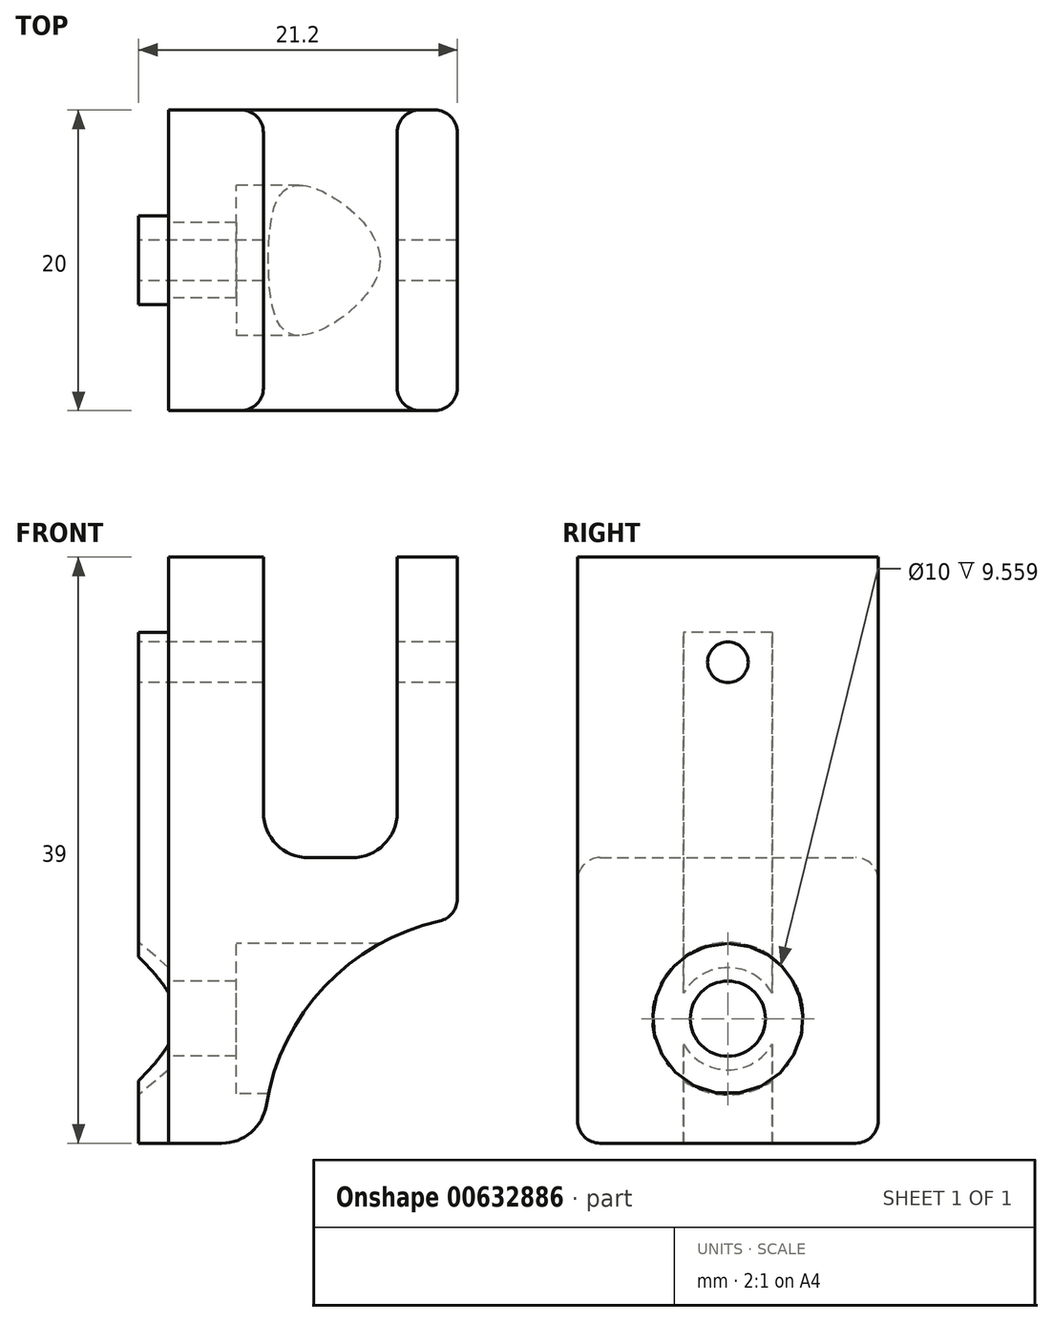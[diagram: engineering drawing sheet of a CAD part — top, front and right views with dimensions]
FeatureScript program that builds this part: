
annotation { "Feature Type Name" : "Feature", "Feature Type Description" : "" }
export const myFeature = defineFeature(function(context is Context, id is Id, definition is map)
    precondition{}
    {
        {
            var Q0;
            Q0=qCreatedBy(makeId("Front.planeOp"),FACE);
            var sketch = newSketch(context, id + "F0", { "sketchPlane" : qUnion([Q0])});
            skLineSegment(sketch, "E0.bottom", {"start": v(0, 0) * mm, "end": v(6.3, 0) * mm});
            skLineSegment(sketch, "E0.right", {"start": v(6.3, 0) * mm, "end": v(6.3, 15) * mm});
            skLineSegment(sketch, "E1.bottom", {"start": v(15.2, 39) * mm, "end": v(19.2, 39) * mm});
            skLineSegment(sketch, "E1.left", {"start": v(15.2, 39) * mm, "end": v(15.2, 19) * mm});
            skLineSegment(sketch, "E2.bottom", {"start": v(15.2, 19) * mm, "end": v(6.3, 19) * mm});
            skLineSegment(sketch, "E2.top", {"start": v(19.2, 15) * mm, "end": v(6.3, 15) * mm});
            skLineSegment(sketch, "E3", {"start": v(19.2, 39) * mm, "end": v(19.2, 15) * mm});
            skLineSegment(sketch, "E4", {"start": v(6.3, 19) * mm, "end": v(6.3, 39) * mm});
            skLineSegment(sketch, "E5", {"start": v(6.3, 39) * mm, "end": v(0, 39) * mm});
            skLineSegment(sketch, "E6", {"start": v(0, 39) * mm, "end": v(0, 0) * mm});
            skSolve(sketch);
        }
        {
            var Q0;
            {var subQ1=sQuery(id+"F0.wireOp",EDGE,"E0.bottom");Q0=makeQuery(id+"F0.imprint","IMPRINT",FACE,{"disambiguationData":[TD([[makeQuery(id+"F0.imprint","IMPRINT",EDGE,{"derivedFrom":subQ1}),1.0]])]});}
            var Q1;
            Q1=makeQuery(id+"F0.imprint","IMPRINT",FACE,{"disambiguationData":[TD([[makeQuery(id+"F0.imprint","IMPRINT",EDGE,{"derivedFrom":sQuery(id+"F0.wireOp",EDGE,"E2.top")}),-1.0]])]});
            var Q2;
            Q2=makeQuery(id+"F0.imprint","IMPRINT",FACE,{"disambiguationData":[TD([[makeQuery(id+"F0.imprint","IMPRINT",EDGE,{"derivedFrom":sQuery(id+"F0.wireOp",EDGE,"E1.bottom")}),-1.0]])]});
            extrude(context, id + "F1", {"entities" : qUnion([Q0, Q1, Q2]), "depth" : 10 * mm, "hasSecondDirection" : true, "secondDirectionOppositeDirection" : true, "secondDirectionDepth" : 10 * mm, "offsetDistance" : 25 * mm});
        }
        {
            var Q0;
            Q0=makeQuery(id+"F1.opExtrude","SWEPT_EDGE",EDGE,{"disambiguationData":[OSD([sQuery(id+"F0.wireOp",EDGE,"E0.right"),sQuery(id+"F0.wireOp",EDGE,"E2.top"),sQuery(id+"F0.wireOp",EDGE,"E2.right")])]});
            fillet(context, id + "F2", {"entities" : qUnion([Q0]), "radius" : 15 * mm, "tangentPropagation" : true, "allowEdgeOverflow" : false});
        }
        {
            var Q0;
            Q0=makeQuery(id+"F1.opExtrude","SWEPT_EDGE",EDGE,{"disambiguationData":[OSD([sQuery(id+"F0.wireOp",EDGE,"E0.right"),sQuery(id+"F0.wireOp",EDGE,"E2.bottom"),sQuery(id+"F0.wireOp",EDGE,"E2.right")])]});
            var Q1;
            Q1=makeQuery(id+"F1.opExtrude","SWEPT_EDGE",EDGE,{"disambiguationData":[OSD([sQuery(id+"F0.wireOp",EDGE,"E1.left"),sQuery(id+"F0.wireOp",EDGE,"E2.bottom")])]});
            fillet(context, id + "F3", {"entities" : qUnion([Q0, Q1]), "radius" : 3 * mm, "tangentPropagation" : true, "allowEdgeOverflow" : false});
        }
        {
            var Q0;
            Q0=qCreatedBy(makeId("Top.planeOp"),FACE);
            var sketch = newSketch(context, id + "F4", { "sketchPlane" : qUnion([Q0])});
            skLineSegment(sketch, "E7.bottom", {"start": v(-2, 2.95) * mm, "end": v(2, 2.95) * mm});
            skLineSegment(sketch, "E7.top", {"start": v(-2, -2.95) * mm, "end": v(2, -2.95) * mm});
            skLineSegment(sketch, "E7.left", {"start": v(-2, 2.95) * mm, "end": v(-2, -2.95) * mm});
            skLineSegment(sketch, "E7.right", {"start": v(2, 2.95) * mm, "end": v(2, -2.95) * mm});
            skPoint(sketch, "E7.middle", {"position": v(0, 0) * mm});
            skSolve(sketch);
        }
        {
            var Q0;
            Q0=makeQuery(id+"F4.imprint","IMPRINT",FACE,{"disambiguationData":[TD([[makeQuery(id+"F4.imprint","IMPRINT",EDGE,{"derivedFrom":sQuery(id+"F4.wireOp",EDGE,"E7.bottom")}),-1.0]])]});
            extrude(context, id + "F5", {"entities" : qUnion([Q0]), "operationType" : NewBodyOperationType.ADD, "depth" : 34 * mm, "offsetDistance" : 25 * mm});
        }
        {
            var Q0;
            Q0=qCreatedBy(makeId("Right.planeOp"),FACE);
            var sketch = newSketch(context, id + "F6", { "sketchPlane" : qUnion([Q0])});
            skCircle(sketch, "E8", {"center": v(0, 32) * mm, "radius": 1.35 * mm});
            skCircle(sketch, "E9", {"center": v(0, 8.28) * mm, "radius": 2.5 * mm});
            skCircle(sketch, "E10", {"center": v(0, 8.28) * mm, "radius": 5 * mm});
            skCircle(sketch, "E11", {"center": v(0, 8.28) * mm, "radius": 3.4 * mm});
            skSolve(sketch);
        }
        {
            var Q0;
            Q0=makeQuery(id+"F6.imprint","IMPRINT",FACE,{"disambiguationData":[TD([[makeQuery(id+"F6.imprint","IMPRINT",EDGE,{"derivedFrom":sQuery(id+"F6.wireOp",EDGE,"E8")}),1.0]])]});
            extrude(context, id + "F7", {"entities" : qUnion([Q0]), "operationType" : NewBodyOperationType.REMOVE, "depth" : 25 * mm, "hasSecondDirection" : true, "secondDirectionOppositeDirection" : true, "secondDirectionDepth" : 25 * mm});
        }
        {
            var Q0;
            Q0=makeQuery(id+"F6.imprint","IMPRINT",FACE,{"disambiguationData":[TD([[makeQuery(id+"F6.imprint","IMPRINT",EDGE,{"derivedFrom":sQuery(id+"F6.wireOp",EDGE,"E9")}),1.0]])]});
            extrude(context, id + "F8", {"entities" : qUnion([Q0]), "operationType" : NewBodyOperationType.REMOVE, "depth" : 15 * mm, "hasSecondDirection" : true, "secondDirectionOppositeDirection" : true, "secondDirectionDepth" : 10 * mm});
        }
        {
            var Q0;
            Q0=makeQuery(id+"F6.imprint","IMPRINT",FACE,{"disambiguationData":[TD([[makeQuery(id+"F6.imprint","IMPRINT",EDGE,{"derivedFrom":sQuery(id+"F6.wireOp",EDGE,"E9")}),-1.0]])]});
            var Q1;
            Q1=makeQuery(id+"F6.imprint","IMPRINT",FACE,{"disambiguationData":[TD([[makeQuery(id+"F6.imprint","IMPRINT",EDGE,{"derivedFrom":sQuery(id+"F6.wireOp",EDGE,"E10")}),1.0]])]});
            extrude(context, id + "F9", {"entities" : qUnion([Q0, Q1]), "operationType" : NewBodyOperationType.REMOVE, "depth" : 30 * mm, "hasSecondDirection" : true, "secondDirectionOppositeDirection" : false, "secondDirectionDepth" : 4.5 * mm, "offsetDistance" : 25 * mm});
        }
        {
            var Q0;
            Q0=makeQuery(id+"F6.imprint","IMPRINT",FACE,{"disambiguationData":[TD([[makeQuery(id+"F6.imprint","IMPRINT",EDGE,{"derivedFrom":sQuery(id+"F6.wireOp",EDGE,"E9")}),-1.0]])]});
            extrude(context, id + "F10", {"entities" : qUnion([Q0]), "operationType" : NewBodyOperationType.REMOVE, "oppositeDirection" : true, "depth" : 10 * mm, "hasDraft" : true, "draftAngle" : 40 * degree, "offsetDistance" : 25 * mm});
        }
        {
            var Q0;
            Q0=makeQuery(id+"FVQzFijdfIberP7_1.boolean.opBoolean","INTERSECT",EDGE,{"derivedFrom":[makeQuery(id+"F1.opExtrude","SWEPT_FACE",FACE,{"disambiguationData":[OSD([sQuery(id+"F0.wireOp",EDGE,"E1.bottom")])]}),makeQuery(id+"FVQzFijdfIberP7_1.opExtrude","SWEPT_FACE",FACE,{"disambiguationData":[OSD([sQuery(id+"FllVCIRI6JCQqES_1.wireOp",EDGE,"0gJeJJ1y-EJvm-fnZg-GKMm-UuW6JYeC1a1f")])]})]});
            var Q1;
            Q1=makeQuery(id+"F1.opExtrude","CAP_EDGE",EDGE,{"disambiguationData":[OSD([sQuery(id+"F0.wireOp",EDGE,"E0.top")])],"isStart":true});
            var Q2;
            Q2=makeQuery(id+"FVQzFijdfIberP7_1.boolean.opBoolean","INTERSECT",EDGE,{"derivedFrom":[makeQuery(id+"F1.opExtrude","SWEPT_FACE",FACE,{"disambiguationData":[OSD([sQuery(id+"F0.wireOp",EDGE,"E1.bottom")])]}),makeQuery(id+"FVQzFijdfIberP7_1.opExtrude","SWEPT_FACE",FACE,{"disambiguationData":[OSD([sQuery(id+"FllVCIRI6JCQqES_1.wireOp",EDGE,"ad4fdd70-2fb9-4313-b07b-df9d61838bc60.MirrorCS")])]})]});
            var Q3;
            Q3=makeQuery(id+"F1.opExtrude","CAP_EDGE",EDGE,{"disambiguationData":[OSD([sQuery(id+"F0.wireOp",EDGE,"E0.top")])],"isStart":false});
            var Q4;
            Q4=makeQuery(id+"F1.opExtrude","CAP_EDGE",EDGE,{"disambiguationData":[OSD([sQuery(id+"F0.wireOp",EDGE,"E0.bottom")])],"isStart":true});
            var Q5;
            Q5=makeQuery(id+"F1.opExtrude","CAP_EDGE",EDGE,{"disambiguationData":[OSD([sQuery(id+"F0.wireOp",EDGE,"E0.bottom")])],"isStart":false});
            var Q6;
            Q6=makeQuery(id+"F2.opFillet","BLEND_EDGE",EDGE,{"blendedFrom":[makeQuery(id+"F1.opExtrude","SWEPT_EDGE",EDGE,{"disambiguationData":[OSD([sQuery(id+"F0.wireOp",EDGE,"E0.right"),sQuery(id+"F0.wireOp",EDGE,"E2.top"),sQuery(id+"F0.wireOp",EDGE,"E2.right")])]}),makeQuery(id+"F1.opExtrude","SWEPT_FACE",FACE,{"disambiguationData":[OSD([sQuery(id+"F0.wireOp",EDGE,"E1.right"),sQuery(id+"F0.wireOp",EDGE,"E2.left")])]})],"blendedInto":[makeQuery(id+"F1.opExtrude","SWEPT_FACE",FACE,{"disambiguationData":[OSD([sQuery(id+"F0.wireOp",EDGE,"E1.right"),sQuery(id+"F0.wireOp",EDGE,"E2.left")])]})]});
            var Q7;
            Q7=makeQuery(id+"FVQzFijdfIberP7_1.boolean.opBoolean","INTERSECT",EDGE,{"derivedFrom":[makeQuery(id+"F2.opFillet","BLEND_FACE",FACE,{"disambiguationData":[OSD([sQuery(id+"F0.wireOp",EDGE,"E0.right"),sQuery(id+"F0.wireOp",EDGE,"E2.top"),sQuery(id+"F0.wireOp",EDGE,"E2.right")])]}),makeQuery(id+"FVQzFijdfIberP7_1.opExtrude","SWEPT_FACE",FACE,{"disambiguationData":[OSD([sQuery(id+"FllVCIRI6JCQqES_1.wireOp",EDGE,"ad4fdd70-2fb9-4313-b07b-df9d61838bc60.MirrorCS")])]})]});
            var Q8;
            Q8=makeQuery(id+"FVQzFijdfIberP7_1.boolean.opBoolean","COPY",EDGE,{"derivedFrom":makeQuery(id+"FVQzFijdfIberP7_1.opExtrude","SWEPT_EDGE",EDGE,{"disambiguationData":[OSD([sQuery(id+"FllVCIRI6JCQqES_1.wireOp",EDGE,"ad4fdd70-2fb9-4313-b07b-df9d61838bc60.MirrorCS"),sQuery(id+"FllVCIRI6JCQqES_1.wireOp",EDGE,"6d596fc3-1ca0-40c5-aee4-fe9f60dd68ae0.MirrorCS")])]})});
            var Q9;
            Q9=makeQuery(id+"FVQzFijdfIberP7_1.boolean.opBoolean","COPY",EDGE,{"derivedFrom":makeQuery(id+"FVQzFijdfIberP7_1.opExtrude","SWEPT_EDGE",EDGE,{"disambiguationData":[OSD([sQuery(id+"FllVCIRI6JCQqES_1.wireOp",EDGE,"0gJeJJ1y-EJvm-fnZg-GKMm-UuW6JYeC1a1f"),sQuery(id+"FllVCIRI6JCQqES_1.wireOp",EDGE,"ayhZilKi-yUaR-i3xm-yCP8-kIRGACUT5FV1")])]})});
            var Q10;
            Q10=makeQuery(id+"FVQzFijdfIberP7_1.boolean.opBoolean","INTERSECT",EDGE,{"derivedFrom":[makeQuery(id+"F2.opFillet","BLEND_FACE",FACE,{"disambiguationData":[OSD([sQuery(id+"F0.wireOp",EDGE,"E0.right"),sQuery(id+"F0.wireOp",EDGE,"E2.top"),sQuery(id+"F0.wireOp",EDGE,"E2.right")])]}),makeQuery(id+"FVQzFijdfIberP7_1.opExtrude","SWEPT_FACE",FACE,{"disambiguationData":[OSD([sQuery(id+"FllVCIRI6JCQqES_1.wireOp",EDGE,"0gJeJJ1y-EJvm-fnZg-GKMm-UuW6JYeC1a1f")])]})]});
            var Q11;
            {var subQ0=sQuery(id+"F0.wireOp",EDGE,"E0.right");Q11=makeQuery(id+"F1.opExtrude","CAP_EDGE",EDGE,{"disambiguationData":[OSD([subQ0]),TDD([makeQuery(id+"F0.imprint","IMPRINT",EDGE,{"disambiguationData":[TD([[makeQuery(id+"F0.imprint","INTERSECT",VERTEX,{"derivedFrom":[sQuery(id+"F0.wireOp",EDGE,"E0.top"),subQ0]}),1.0]])],"derivedFrom":subQ0})])],"isStart":false});}
            var Q12;
            Q12=makeQuery(id+"F3.opFillet","BLEND_EDGE",EDGE,{"blendedFrom":[makeQuery(id+"F1.opExtrude","SWEPT_EDGE",EDGE,{"disambiguationData":[OSD([sQuery(id+"F0.wireOp",EDGE,"E1.left"),sQuery(id+"F0.wireOp",EDGE,"E2.bottom")])]}),makeQuery(id+"FVQzFijdfIberP7_1.boolean.opBoolean","COPY",FACE,{"derivedFrom":makeQuery(id+"FVQzFijdfIberP7_1.opExtrude","SWEPT_FACE",FACE,{"disambiguationData":[OSD([sQuery(id+"FllVCIRI6JCQqES_1.wireOp",EDGE,"ad4fdd70-2fb9-4313-b07b-df9d61838bc60.MirrorCS")])]})})],"blendedInto":[makeQuery(id+"FVQzFijdfIberP7_1.boolean.opBoolean","COPY",FACE,{"derivedFrom":makeQuery(id+"FVQzFijdfIberP7_1.opExtrude","SWEPT_FACE",FACE,{"disambiguationData":[OSD([sQuery(id+"FllVCIRI6JCQqES_1.wireOp",EDGE,"ad4fdd70-2fb9-4313-b07b-df9d61838bc60.MirrorCS")])]})})]});
            var Q13;
            Q13=makeQuery(id+"FVQzFijdfIberP7_1.boolean.opBoolean","INTERSECT",EDGE,{"derivedFrom":[makeQuery(id+"F1.opExtrude","SWEPT_FACE",FACE,{"disambiguationData":[OSD([sQuery(id+"F0.wireOp",EDGE,"E2.bottom")])]}),makeQuery(id+"FVQzFijdfIberP7_1.opExtrude","SWEPT_FACE",FACE,{"disambiguationData":[OSD([sQuery(id+"FllVCIRI6JCQqES_1.wireOp",EDGE,"0gJeJJ1y-EJvm-fnZg-GKMm-UuW6JYeC1a1f")])]})]});
            var Q14;
            {var subQ0=sQuery(id+"F0.wireOp",EDGE,"E0.right");Q14=makeQuery(id+"F1.opExtrude","CAP_EDGE",EDGE,{"disambiguationData":[OSD([subQ0]),TDD([makeQuery(id+"F0.imprint","IMPRINT",EDGE,{"disambiguationData":[TD([[makeQuery(id+"F0.imprint","INTERSECT",VERTEX,{"derivedFrom":[sQuery(id+"F0.wireOp",EDGE,"E0.top"),subQ0]}),1.0]])],"derivedFrom":subQ0})])],"isStart":true});}
            var Q15;
            {var subQ0=sQuery(id+"F0.wireOp",EDGE,"E0.right");var subQ1=sQuery(id+"F0.wireOp",EDGE,"E2.right");var subQ2=sQuery(id+"F0.wireOp",EDGE,"E2.top");Q15=makeQuery(id+"F2.opFillet","BLEND_EDGE",EDGE,{"blendedFrom":[makeQuery(id+"F1.opExtrude","SWEPT_EDGE",EDGE,{"disambiguationData":[OSD([subQ0,subQ2,subQ1])]}),makeQuery(id+"F1.opExtrude","SWEPT_FACE",FACE,{"disambiguationData":[OSD([subQ0]),TDD([makeQuery(id+"F0.imprint","IMPRINT",EDGE,{"disambiguationData":[TD([[makeQuery(id+"F0.imprint","INTERSECT",VERTEX,{"derivedFrom":[sQuery(id+"F0.wireOp",EDGE,"E0.bottom"),subQ0]}),-1.0]])],"derivedFrom":subQ0})])]})],"blendedInto":[makeQuery(id+"F1.opExtrude","SWEPT_FACE",FACE,{"disambiguationData":[OSD([subQ0]),TDD([makeQuery(id+"F0.imprint","IMPRINT",EDGE,{"disambiguationData":[TD([[makeQuery(id+"F0.imprint","INTERSECT",VERTEX,{"derivedFrom":[sQuery(id+"F0.wireOp",EDGE,"E0.bottom"),subQ0]}),-1.0]])],"derivedFrom":subQ0})])]})]});}
            var Q16;
            Q16=makeQuery(id+"F2.opFillet","BLEND_EDGE",EDGE,{"blendedFrom":[makeQuery(id+"F1.opExtrude","SWEPT_EDGE",EDGE,{"disambiguationData":[OSD([sQuery(id+"F0.wireOp",EDGE,"E0.right"),sQuery(id+"F0.wireOp",EDGE,"E2.top")])]}),makeQuery(id+"F1.opExtrude","SWEPT_FACE",FACE,{"disambiguationData":[OSD([sQuery(id+"F0.wireOp",EDGE,"E3")])]})],"blendedInto":[makeQuery(id+"F1.opExtrude","SWEPT_FACE",FACE,{"disambiguationData":[OSD([sQuery(id+"F0.wireOp",EDGE,"E3")])]})]});
            var Q17;
            Q17=makeQuery(id+"F1.opExtrude","CAP_EDGE",EDGE,{"disambiguationData":[OSD([sQuery(id+"F0.wireOp",EDGE,"E3")])],"isStart":false});
            var Q18;
            Q18=makeQuery(id+"F1.opExtrude","CAP_EDGE",EDGE,{"disambiguationData":[OSD([sQuery(id+"F0.wireOp",EDGE,"E3")])],"isStart":true});
            var Q19;
            Q19=makeQuery(id+"F1.opExtrude","CAP_EDGE",EDGE,{"disambiguationData":[OSD([sQuery(id+"F0.wireOp",EDGE,"E1.left")])],"isStart":true});
            var Q20;
            Q20=makeQuery(id+"F1.opExtrude","CAP_EDGE",EDGE,{"disambiguationData":[OSD([sQuery(id+"F0.wireOp",EDGE,"E4")])],"isStart":false});
            fillet(context, id + "F11", {"entities" : qUnion([Q0, Q1, Q2, Q3, Q4, Q5, Q6, Q7, Q8, Q9, Q10, Q11, Q12, Q13, Q14, Q15, Q16, Q17, Q18, Q19, Q20]), "radius" : 1.5 * mm, "tangentPropagation" : true, "allowEdgeOverflow" : false});
        }
    });
